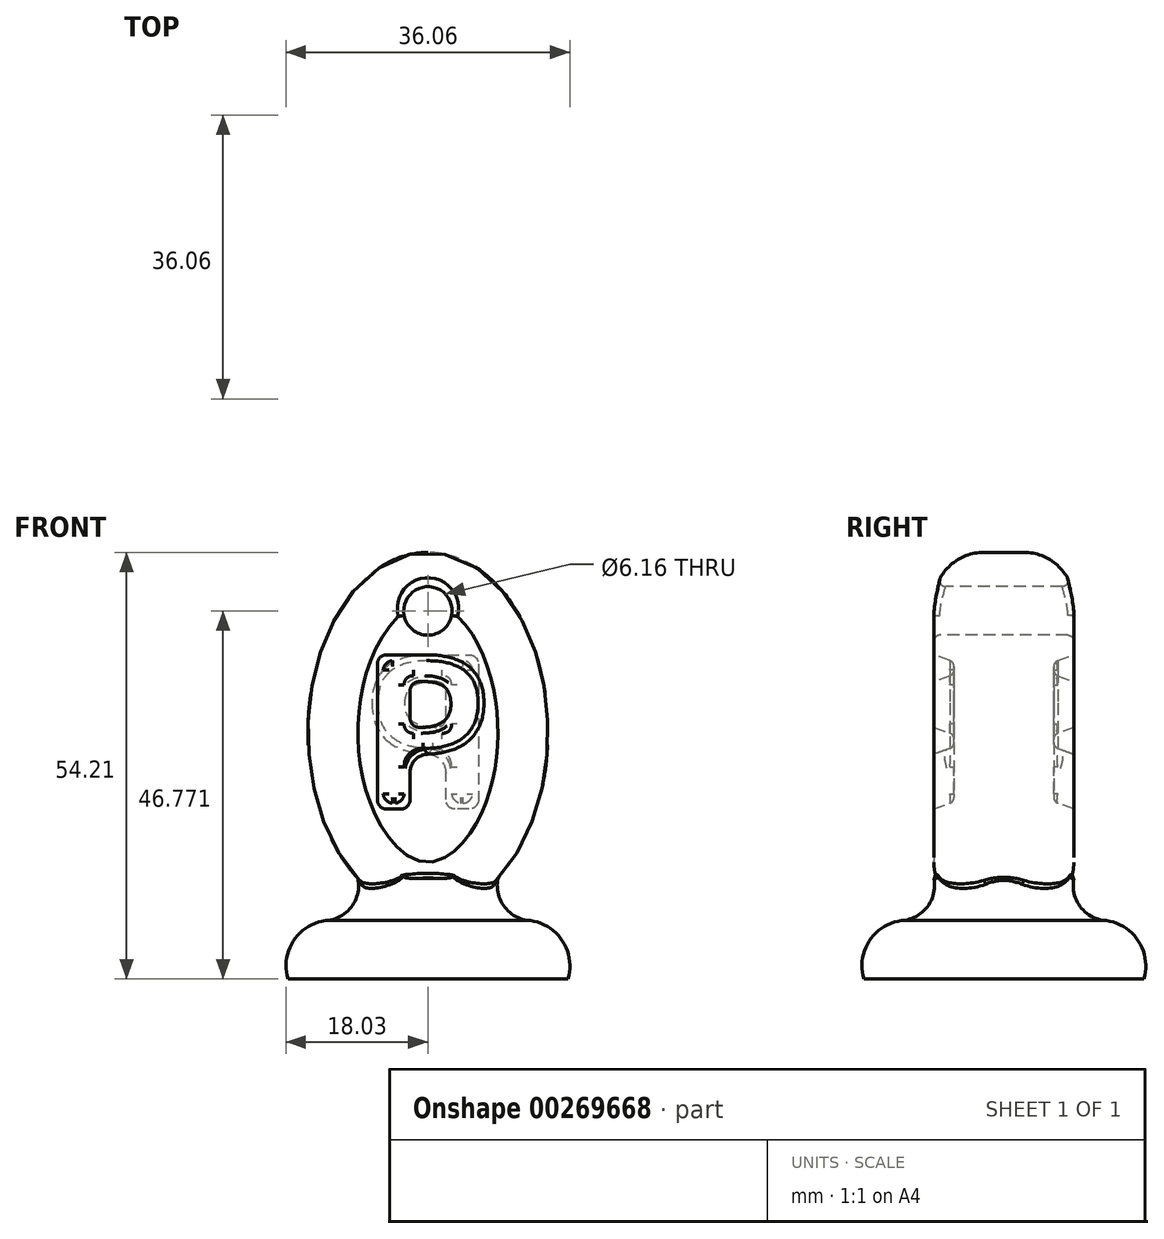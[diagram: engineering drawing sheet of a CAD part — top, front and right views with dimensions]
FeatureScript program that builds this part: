
annotation { "Feature Type Name" : "Feature", "Feature Type Description" : "" }
export const myFeature = defineFeature(function(context is Context, id is Id, definition is map)
    precondition{}
    {
        {
            var Q0;
            Q0=qCreatedBy(makeId("Front.planeOp"),FACE);
            var sketch = newSketch(context, id + "F0", { "sketchPlane" : qUnion([Q0])});
            skEllipse(sketch, "E0", {"center": v(0, 31.35) * mm, "majorRadius": 22.86 * mm, "minorRadius": 15.24 * mm, "majorAxis": v(0, -1)});
            skLineSegment(sketch, "E1", {"start": v(0, 0) * mm, "end": v(0, 8.49) * mm, "construction": true});
            skSolve(sketch);
        }
        {
            var Q0;
            Q0=qSketchRegion(id+"F0",true);
            extrude(context, id + "F1", {"entities" : qUnion([Q0]), "depth" : 8.9 * mm});
        }
        {
            var Q0;
            Q0=makeQuery(id+"F1.opExtrude","CAP_EDGE",EDGE,{"disambiguationData":[OSD([sQuery(id+"F0.wireOp",EDGE,"E0")])],"isStart":false});
            fillet(context, id + "F2", {"entities" : qUnion([Q0]), "radius" : 6.35 * mm, "tangentPropagation" : true, "allowEdgeOverflow" : false});
        }
        {
            var Q0;
            Q0=qCreatedBy(makeId("Front.planeOp"),FACE);
            var sketch = newSketch(context, id + "F3", { "sketchPlane" : qUnion([Q0])});
            skLineSegment(sketch, "E2", {"start": v(0, 0) * mm, "end": v(-17.78, 0) * mm});
            skLineSegment(sketch, "E3", {"start": v(-17.78, 0) * mm, "end": v(0, 25.56) * mm});
            skLineSegment(sketch, "E4", {"start": v(0, 25.56) * mm, "end": v(0, 0) * mm});
            skArc(sketch, "E5", {"start": v(-12.58, 7.48) * mm, "mid": v(-16.99, 5) * mm, "end": v(-17.78, 0) * mm});
            skArc(sketch, "E6", {"start": v(-12.58, 7.48) * mm, "mid": v(-9.6, 9.34) * mm, "end": v(-8.9, 12.78) * mm});
            skLineSegment(sketch, "E7", {"start": v(0, 0) * mm, "end": v(0, -19.3) * mm, "construction": true});
            skSolve(sketch);
        }
        {
            var Q0;
            {var subQ0=sQuery(id+"F3.wireOp",EDGE,"E5");Q0=makeQuery(id+"F3.imprint","IMPRINT",FACE,{"disambiguationData":[TD([[makeQuery(id+"F3.imprint","IMPRINT",EDGE,{"derivedFrom":subQ0}),1.0]])]});}
            var Q1;
            {var subQ4=sQuery(id+"F3.wireOp",EDGE,"E2");Q1=makeQuery(id+"F3.imprint","IMPRINT",FACE,{"disambiguationData":[TD([[makeQuery(id+"F3.imprint","IMPRINT",EDGE,{"derivedFrom":subQ4}),-1.0]])]});}
            var Q2;
            Q2=sQuery(id+"F3.wireOp",EDGE,"E7");
            revolve(context, id + "F4", {"entities" : qUnion([Q0, Q1]), "axis" : qUnion([Q2]), "revolveType" : RevolveType.ONE_DIRECTION, "oppositeDirection" : true, "angle" : 180 * degree});
        }
        {
            var Q0;
            Q0=makeQuery(id+"F1.opExtrude","CAP_FACE",FACE,{"disambiguationData":[OSD([sQuery(id+"F0.wireOp",EDGE,"E0")])],"isStart":false});
            var sketch = newSketch(context, id + "F5", { "sketchPlane" : qUnion([Q0])});
            skSolve(sketch);
        }
        {
            var Q0;
            {var subQ0=sQuery(id+"F0.wireOp",EDGE,"E0");Q0=makeQuery(id+"F5.imprint","IMPRINT",FACE,{"disambiguationData":[TD([[makeQuery(id+"F5.imprint","IMPRINT",EDGE,{"derivedFrom":makeQuery(id+"F2.opFillet","BLEND_EDGE",EDGE,{"blendedFrom":[makeQuery(id+"F1.opExtrude","CAP_EDGE",EDGE,{"disambiguationData":[OSD([subQ0])],"isStart":false}),makeQuery(id+"F1.opExtrude","CAP_FACE",FACE,{"disambiguationData":[OSD([subQ0])],"isStart":false})],"blendedInto":[makeQuery(id+"F1.opExtrude","CAP_FACE",FACE,{"disambiguationData":[OSD([subQ0])],"isStart":false})]})}),1.0]])]});}
            var sketch = newSketch(context, id + "F6", { "sketchPlane" : qUnion([Q0])});
            skText(sketch, "E8", { "text": "P", "fontName": "OpenSans-Bold.ttf"});
            const initialGuessF6  = {"E8": [-0.00889, 0.0216, 1, 0, 0.01976]};
            skSetInitialGuess(sketch, initialGuessF6);
            skSolve(sketch);
        }
        {
            var Q0;
            Q0=qSketchRegion(id+"F6",true);
            extrude(context, id + "F7", {"entities" : qUnion([Q0]), "operationType" : NewBodyOperationType.REMOVE, "oppositeDirection" : true, "depth" : 2.54 * mm, "hasDraft" : true, "draftAngle" : 20 * degree, "draftPullDirection" : true});
        }
        {
            var Q0;
            Q0=makeQuery(id+"F7.boolean.opBoolean","COPY",EDGE,{"derivedFrom":makeQuery(id+"F7.opExtrude","SWEPT_EDGE",EDGE,{"disambiguationData":[OSD([sQuery(id+"F6.wireOp",EDGE,"E8.sketch_text.stroke-9"),sQuery(id+"F6.wireOp",EDGE,"E8.sketch_text.stroke-10")])]})});
            fillet(context, id + "F8", {"entities" : qUnion([Q0]), "radius" : 2.54 * mm, "tangentPropagation" : true, "allowEdgeOverflow" : false});
        }
        {
            var Q0;
            Q0=makeQuery(id+"F7.boolean.opBoolean","COPY",EDGE,{"derivedFrom":makeQuery(id+"F7.opExtrude","SWEPT_EDGE",EDGE,{"disambiguationData":[OSD([sQuery(id+"F6.wireOp",EDGE,"E8.sketch_text.stroke-11"),sQuery(id+"F6.wireOp",EDGE,"E8.sketch_text.stroke-12")])]})});
            var Q1;
            Q1=makeQuery(id+"F7.boolean.opBoolean","COPY",EDGE,{"derivedFrom":makeQuery(id+"F7.opExtrude","SWEPT_EDGE",EDGE,{"disambiguationData":[OSD([sQuery(id+"F6.wireOp",EDGE,"E8.sketch_text.stroke-10"),sQuery(id+"F6.wireOp",EDGE,"E8.sketch_text.stroke-11")])]})});
            var Q2;
            Q2=makeQuery(id+"F7.boolean.opBoolean","COPY",EDGE,{"derivedFrom":makeQuery(id+"F7.opExtrude","SWEPT_EDGE",EDGE,{"disambiguationData":[OSD([sQuery(id+"F6.wireOp",EDGE,"E8.sketch_text.stroke-0"),sQuery(id+"F6.wireOp",EDGE,"E8.sketch_text.stroke-6")])]})});
            var Q3;
            Q3=makeQuery(id+"F7.boolean.opBoolean","COPY",EDGE,{"derivedFrom":makeQuery(id+"F7.opExtrude","SWEPT_EDGE",EDGE,{"disambiguationData":[OSD([sQuery(id+"F6.wireOp",EDGE,"E8.sketch_text.stroke-5"),sQuery(id+"F6.wireOp",EDGE,"E8.sketch_text.stroke-6")])]})});
            var Q4;
            Q4=makeQuery(id+"F7.boolean.opBoolean","COPY",EDGE,{"derivedFrom":makeQuery(id+"F7.opExtrude","SWEPT_EDGE",EDGE,{"disambiguationData":[OSD([sQuery(id+"F6.wireOp",EDGE,"E8.sketch_text.stroke-12"),sQuery(id+"F6.wireOp",EDGE,"E8.sketch_text.stroke-13")])]})});
            fillet(context, id + "F9", {"entities" : qUnion([Q0, Q1, Q2, Q3, Q4]), "radius" : 1.27 * mm, "tangentPropagation" : true, "allowEdgeOverflow" : false});
        }
        {
            var Q0;
            Q0=makeQuery(id+"F7.boolean.opBoolean","COPY",EDGE,{"derivedFrom":makeQuery(id+"F7.opExtrude","CAP_EDGE",EDGE,{"disambiguationData":[OSD([sQuery(id+"F6.wireOp",EDGE,"E8.sketch_text.stroke-6")])],"isStart":false})});
            var Q1;
            Q1=makeQuery(id+"F7.boolean.opBoolean","COPY",EDGE,{"derivedFrom":makeQuery(id+"F7.opExtrude","CAP_EDGE",EDGE,{"disambiguationData":[OSD([sQuery(id+"F6.wireOp",EDGE,"E8.sketch_text.stroke-7")])],"isStart":false})});
            fillet(context, id + "F10", {"entities" : qUnion([Q0, Q1]), "radius" : 0.76 * mm, "tangentPropagation" : true, "allowEdgeOverflow" : false});
        }
        {
            var Q0;
            Q0=makeQuery(id+"F4.opRevolve","SWEPT_BODY",BODY,{"disambiguationData":[OSD([sQuery(id+"F3.wireOp",EDGE,"E2"),sQuery(id+"F3.wireOp",EDGE,"E3"),sQuery(id+"F3.wireOp",EDGE,"E4"),sQuery(id+"F3.wireOp",EDGE,"E5"),sQuery(id+"F3.wireOp",EDGE,"E6")])]});
            var Q1;
            Q1=makeQuery(id+"F1.opExtrude","SWEPT_BODY",BODY,{"disambiguationData":[OSD([sQuery(id+"F0.wireOp",EDGE,"E0")])]});
            booleanBodies(context, id + "F11", {"operationType" : BooleanOperationType.UNION, "tools" : qUnion([Q0, Q1])});
        }
        {
            var Q0;
            Q0=makeQuery(id+"F4.opRevolve","SWEPT_BODY",BODY,{"disambiguationData":[OSD([sQuery(id+"F3.wireOp",EDGE,"E2"),sQuery(id+"F3.wireOp",EDGE,"E3"),sQuery(id+"F3.wireOp",EDGE,"E4"),sQuery(id+"F3.wireOp",EDGE,"E5"),sQuery(id+"F3.wireOp",EDGE,"E6")])]});
            var Q1;
            Q1=sQuery(id+"F3.wireOp",EDGE,"E7");
            circularPattern(context, id + "F12", {"operationType" : NewBodyOperationType.ADD, "entities" : qUnion([Q0]), "axis" : qUnion([Q1]), "angle" : 360 * degree, "instanceCount" : 2, "equalSpace" : true});
        }
        {
            var Q0;
            Q0=qCreatedBy(makeId("Front.planeOp"),FACE);
            var sketch = newSketch(context, id + "F13", { "sketchPlane" : qUnion([Q0])});
            skCircle(sketch, "E9", {"center": v(0, 46.77) * mm, "radius": 3.08 * mm});
            skSolve(sketch);
        }
        {
            var Q0;
            Q0 = qSketchRegion(id + "F13", true);
            extrude(context, id + "F14", {"entities" : qUnion([Q0]), "operationType" : NewBodyOperationType.REMOVE, "endBound" : BoundingType.SYMMETRIC, "oppositeDirection" : true, "depth" : 50.8 * mm});
        }
        {
            var Q0;
            Q0=makeQuery(id+"F14.boolean.opBoolean","INTERSECT",EDGE,{"derivedFrom":[makeQuery(id+"F2.opFillet","BLEND_FACE",FACE,{"disambiguationData":[OSD([sQuery(id+"F0.wireOp",EDGE,"E0")])]}),makeQuery(id+"F14.opExtrude","SWEPT_FACE",FACE,{"disambiguationData":[OSD([sQuery(id+"F13.wireOp",EDGE,"E9")])]})]});
            var Q1;
            {var subQ0=sQuery(id+"F0.wireOp",EDGE,"E0");Q1=makeQuery(id+"F14.boolean.opBoolean","INTERSECT",EDGE,{"derivedFrom":[makeQuery(id+"F7.boolean.opBoolean","SPLIT",FACE,{"disambiguationData":[TD([makeQuery(id+"F2.opFillet","BLEND_FACE",FACE,{"disambiguationData":[OSD([subQ0])]})])],"derivedFrom":makeQuery(id+"F1.opExtrude","CAP_FACE",FACE,{"disambiguationData":[OSD([subQ0])],"isStart":false})}),makeQuery(id+"F14.opExtrude","SWEPT_FACE",FACE,{"disambiguationData":[OSD([sQuery(id+"F13.wireOp",EDGE,"E9")])]})]});}
            var Q2;
            {var subQ0=sQuery(id+"F0.wireOp",EDGE,"E0");Q2=makeQuery(id+"F14.boolean.opBoolean","INTERSECT",EDGE,{"derivedFrom":[makeQuery(id+"F12.opPattern","COPY",FACE,{"derivedFrom":makeQuery(id+"F7.boolean.opBoolean","SPLIT",FACE,{"disambiguationData":[TD([makeQuery(id+"F2.opFillet","BLEND_FACE",FACE,{"disambiguationData":[OSD([subQ0])]})])],"derivedFrom":makeQuery(id+"F1.opExtrude","CAP_FACE",FACE,{"disambiguationData":[OSD([subQ0])],"isStart":false})}),"instanceName":"1"}),makeQuery(id+"F14.opExtrude","SWEPT_FACE",FACE,{"disambiguationData":[OSD([sQuery(id+"F13.wireOp",EDGE,"E9")])]})]});}
            var Q3;
            Q3=makeQuery(id+"F14.boolean.opBoolean","INTERSECT",EDGE,{"derivedFrom":[makeQuery(id+"F12.opPattern","COPY",FACE,{"derivedFrom":makeQuery(id+"F2.opFillet","BLEND_FACE",FACE,{"disambiguationData":[OSD([sQuery(id+"F0.wireOp",EDGE,"E0")])]}),"instanceName":"1"}),makeQuery(id+"F14.opExtrude","SWEPT_FACE",FACE,{"disambiguationData":[OSD([sQuery(id+"F13.wireOp",EDGE,"E9")])]})]});
            fillet(context, id + "F15", {"entities" : qUnion([Q0, Q1, Q2, Q3]), "radius" : 0.76 * mm, "tangentPropagation" : true, "allowEdgeOverflow" : false});
        }
        {
            var Q0;
            Q0=makeQuery(id+"F11.opBoolean","INTERSECT",EDGE,{"derivedFrom":[makeQuery(id+"F2.opFillet","BLEND_FACE",FACE,{"disambiguationData":[OSD([sQuery(id+"F0.wireOp",EDGE,"E0")])]}),makeQuery(id+"F4.opRevolve","SWEPT_FACE",FACE,{"disambiguationData":[OSD([sQuery(id+"F3.wireOp",EDGE,"E3")])]})]});
            var Q1;
            Q1=makeQuery(id+"F11.opBoolean","INTERSECT",EDGE,{"disambiguationData":[OD(1.0)],"derivedFrom":[makeQuery(id+"F2.opFillet","BLEND_FACE",FACE,{"disambiguationData":[OSD([sQuery(id+"F0.wireOp",EDGE,"E0")])]}),makeQuery(id+"F4.opRevolve","SWEPT_FACE",FACE,{"disambiguationData":[OSD([sQuery(id+"F3.wireOp",EDGE,"E6")])]})]});
            var Q2;
            {var subQ0=makeQuery(id+"F4.opRevolve","SWEPT_FACE",FACE,{"disambiguationData":[OSD([sQuery(id+"F3.wireOp",EDGE,"E6")])]});var subQ1=makeQuery(id+"F1.opExtrude","SWEPT_FACE",FACE,{"disambiguationData":[OSD([sQuery(id+"F0.wireOp",EDGE,"E0")])]});Q2=makeQuery(id+"F12.boolean.opBoolean","MERGE",EDGE,{"derivedFrom":[makeQuery(id+"F11.opBoolean","INTERSECT",EDGE,{"disambiguationData":[OD(1.0)],"derivedFrom":[subQ1,subQ0]}),makeQuery(id+"F12.opPattern","COPY",EDGE,{"derivedFrom":makeQuery(id+"F11.opBoolean","INTERSECT",EDGE,{"disambiguationData":[OD(0.0)],"derivedFrom":[subQ1,subQ0]}),"instanceName":"1"})]});}
            var Q3;
            Q3=makeQuery(id+"F12.opPattern","COPY",EDGE,{"derivedFrom":makeQuery(id+"F11.opBoolean","INTERSECT",EDGE,{"disambiguationData":[OD(0.0)],"derivedFrom":[makeQuery(id+"F2.opFillet","BLEND_FACE",FACE,{"disambiguationData":[OSD([sQuery(id+"F0.wireOp",EDGE,"E0")])]}),makeQuery(id+"F4.opRevolve","SWEPT_FACE",FACE,{"disambiguationData":[OSD([sQuery(id+"F3.wireOp",EDGE,"E6")])]})]}),"instanceName":"1"});
            var Q4;
            Q4=makeQuery(id+"F12.opPattern","COPY",EDGE,{"derivedFrom":makeQuery(id+"F11.opBoolean","INTERSECT",EDGE,{"derivedFrom":[makeQuery(id+"F2.opFillet","BLEND_FACE",FACE,{"disambiguationData":[OSD([sQuery(id+"F0.wireOp",EDGE,"E0")])]}),makeQuery(id+"F4.opRevolve","SWEPT_FACE",FACE,{"disambiguationData":[OSD([sQuery(id+"F3.wireOp",EDGE,"E3")])]})]}),"instanceName":"1"});
            var Q5;
            Q5=makeQuery(id+"F12.opPattern","COPY",EDGE,{"derivedFrom":makeQuery(id+"F11.opBoolean","INTERSECT",EDGE,{"disambiguationData":[OD(1.0)],"derivedFrom":[makeQuery(id+"F2.opFillet","BLEND_FACE",FACE,{"disambiguationData":[OSD([sQuery(id+"F0.wireOp",EDGE,"E0")])]}),makeQuery(id+"F4.opRevolve","SWEPT_FACE",FACE,{"disambiguationData":[OSD([sQuery(id+"F3.wireOp",EDGE,"E6")])]})]}),"instanceName":"1"});
            var Q6;
            {var subQ0=makeQuery(id+"F4.opRevolve","SWEPT_FACE",FACE,{"disambiguationData":[OSD([sQuery(id+"F3.wireOp",EDGE,"E6")])]});var subQ1=makeQuery(id+"F1.opExtrude","SWEPT_FACE",FACE,{"disambiguationData":[OSD([sQuery(id+"F0.wireOp",EDGE,"E0")])]});Q6=makeQuery(id+"F12.boolean.opBoolean","MERGE",EDGE,{"derivedFrom":[makeQuery(id+"F11.opBoolean","INTERSECT",EDGE,{"disambiguationData":[OD(0.0)],"derivedFrom":[subQ1,subQ0]}),makeQuery(id+"F12.opPattern","COPY",EDGE,{"derivedFrom":makeQuery(id+"F11.opBoolean","INTERSECT",EDGE,{"disambiguationData":[OD(1.0)],"derivedFrom":[subQ1,subQ0]}),"instanceName":"1"})]});}
            fillet(context, id + "F16", {"entities" : qUnion([Q0, Q1, Q2, Q3, Q4, Q5, Q6]), "radius" : 0.76 * mm, "tangentPropagation" : true, "allowEdgeOverflow" : false});
        }
    });
